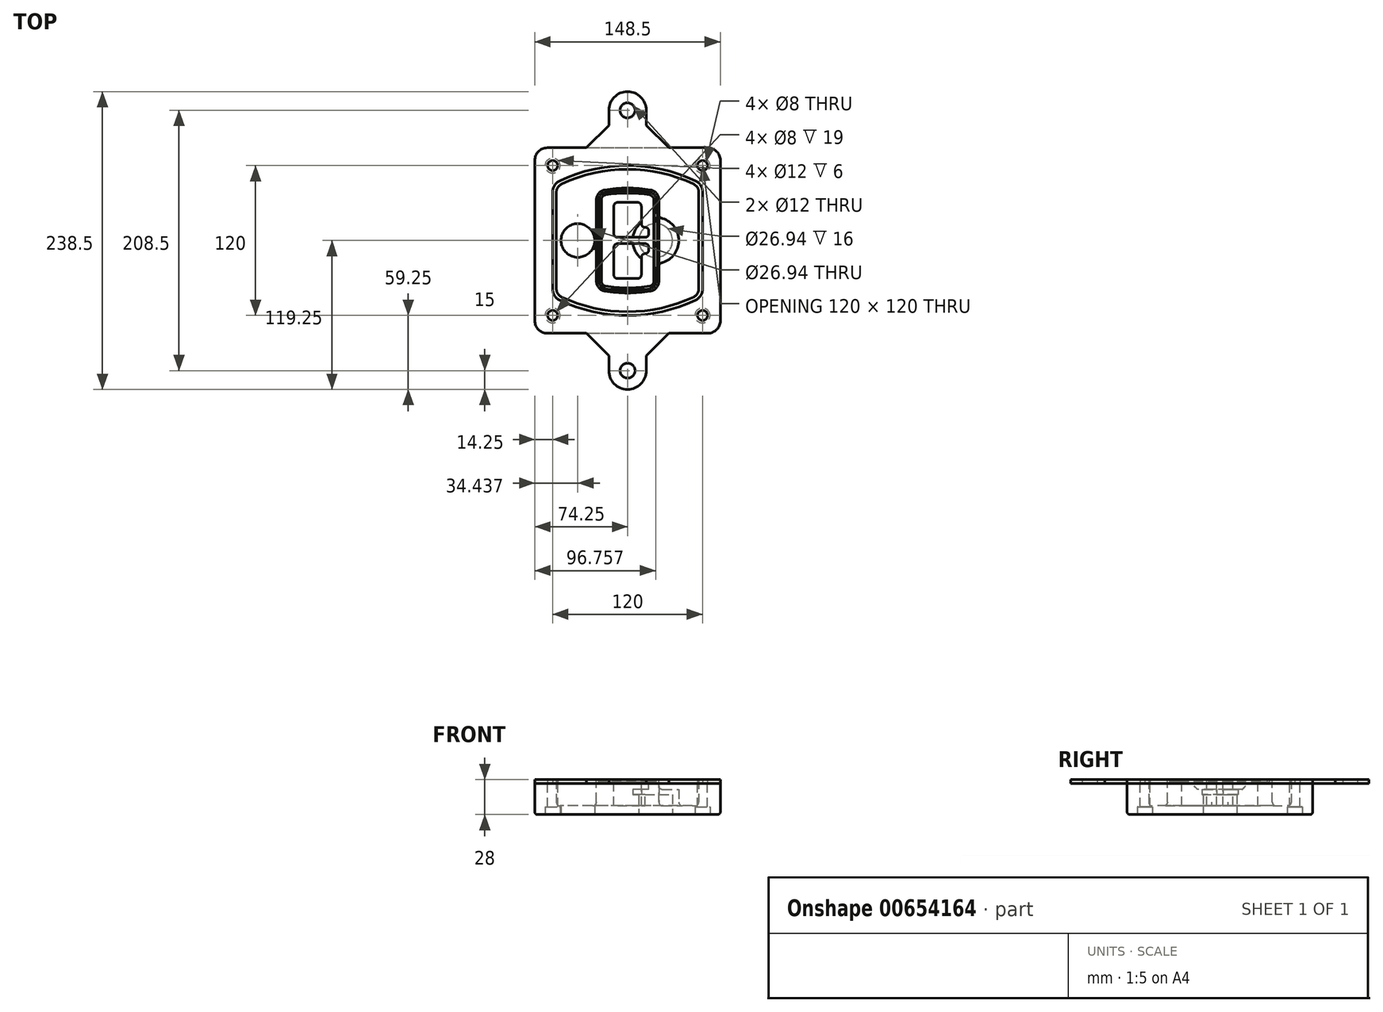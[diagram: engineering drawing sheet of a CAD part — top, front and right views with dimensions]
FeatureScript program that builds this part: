
annotation { "Feature Type Name" : "Feature", "Feature Type Description" : "" }
export const myFeature = defineFeature(function(context is Context, id is Id, definition is map)
    precondition{}
    {
        {
            var Q0;
            Q0=qCreatedBy(makeId("Top.planeOp"),FACE);
            var sketch = newSketch(context, id + "F0", { "sketchPlane" : qUnion([Q0])});
            skPoint(sketch, "E0.rect.middle", {"position": v(0, 0) * mm});
            skLineSegment(sketch, "E1.bottom", {"start": v(-64.25, -74.25) * mm, "end": v(64.25, -74.25) * mm});
            skLineSegment(sketch, "E1.top", {"start": v(-64.25, 74.25) * mm, "end": v(64.25, 74.25) * mm});
            skLineSegment(sketch, "E1.left", {"start": v(-74.25, -64.25) * mm, "end": v(-74.25, 64.25) * mm});
            skLineSegment(sketch, "E1.right", {"start": v(74.25, -64.25) * mm, "end": v(74.25, 64.25) * mm});
            skLineSegment(sketch, "E2", {"start": v(-74.25, 74.25) * mm, "end": v(74.25, -74.25) * mm, "construction": true});
            skLineSegment(sketch, "E3", {"start": v(74.25, 74.25) * mm, "end": v(-74.25, -74.25) * mm, "construction": true});
            skCircle(sketch, "E4", {"center": v(-60, 60) * mm, "radius": 4 * mm});
            skCircle(sketch, "E5", {"center": v(60, 60) * mm, "radius": 4 * mm});
            skCircle(sketch, "E6", {"center": v(60, -60) * mm, "radius": 4 * mm});
            skCircle(sketch, "E7", {"center": v(-60, -60) * mm, "radius": 4 * mm});
            skLineSegment(sketch, "E8", {"start": v(-60, 60) * mm, "end": v(60, 60) * mm, "construction": true});
            skLineSegment(sketch, "E9", {"start": v(60, 60) * mm, "end": v(60, -60) * mm, "construction": true});
            skLineSegment(sketch, "E10", {"start": v(60, -60) * mm, "end": v(-60, -60) * mm, "construction": true});
            skLineSegment(sketch, "E11", {"start": v(-60, -60) * mm, "end": v(-60, 60) * mm, "construction": true});
            skLineSegment(sketch, "E12", {"start": v(-60, 38.83) * mm, "end": v(-60, -38.83) * mm});
            skLineSegment(sketch, "E13", {"start": v(60, 38.83) * mm, "end": v(60, -38.83) * mm});
            skArc(sketch, "E14", {"start": v(54.26, 47.88) * mm, "mid": v(0, 60) * mm, "end": v(-54.26, 47.88) * mm});
            skArc(sketch, "E15", {"start": v(-54.26, -47.88) * mm, "mid": v(0, -60) * mm, "end": v(54.26, -47.88) * mm});
            skLineSegment(sketch, "E16", {"start": v(-60, 0) * mm, "end": v(60, 0) * mm, "construction": true});
            skPoint(sketch, "E17.visualSharp", {"position": v(-60, -45) * mm});
            skArc(sketch, "E17.filletArc", {"start": v(-60, -38.83) * mm, "mid": v(-58.44, -44.2) * mm, "end": v(-54.26, -47.88) * mm});
            skPoint(sketch, "E18.visualSharp", {"position": v(-60, 45) * mm});
            skArc(sketch, "E18.filletArc", {"start": v(-54.26, 47.88) * mm, "mid": v(-58.44, 44.2) * mm, "end": v(-60, 38.83) * mm});
            skPoint(sketch, "E19.visualSharp", {"position": v(60, 45) * mm});
            skArc(sketch, "E19.filletArc", {"start": v(60, 38.83) * mm, "mid": v(58.44, 44.2) * mm, "end": v(54.26, 47.88) * mm});
            skPoint(sketch, "E20.visualSharp", {"position": v(60, -45) * mm});
            skArc(sketch, "E20.filletArc", {"start": v(54.26, -47.88) * mm, "mid": v(58.44, -44.2) * mm, "end": v(60, -38.83) * mm});
            skPoint(sketch, "E21.visualSharp", {"position": v(-74.25, 74.25) * mm});
            skArc(sketch, "E21.filletArc", {"start": v(-64.25, 74.25) * mm, "mid": v(-71.32, 71.32) * mm, "end": v(-74.25, 64.25) * mm});
            skPoint(sketch, "E22.visualSharp", {"position": v(74.25, 74.25) * mm});
            skArc(sketch, "E22.filletArc", {"start": v(74.25, 64.25) * mm, "mid": v(71.32, 71.32) * mm, "end": v(64.25, 74.25) * mm});
            skPoint(sketch, "E23.visualSharp", {"position": v(74.25, -74.25) * mm});
            skArc(sketch, "E23.filletArc", {"start": v(64.25, -74.25) * mm, "mid": v(71.32, -71.32) * mm, "end": v(74.25, -64.25) * mm});
            skPoint(sketch, "E24.visualSharp", {"position": v(-74.25, -74.25) * mm});
            skArc(sketch, "E24.filletArc", {"start": v(-74.25, -64.25) * mm, "mid": v(-71.32, -71.32) * mm, "end": v(-64.25, -74.25) * mm});
            skArc(sketch, "E25.0", {"start": v(57, 38.83) * mm, "mid": v(55.9, 42.58) * mm, "end": v(52.98, 45.17) * mm});
            skLineSegment(sketch, "E25.1", {"start": v(57, 38.83) * mm, "end": v(57, -38.83) * mm});
            skArc(sketch, "E25.2", {"start": v(52.98, -45.17) * mm, "mid": v(55.9, -42.58) * mm, "end": v(57, -38.83) * mm});
            skArc(sketch, "E25.3", {"start": v(-52.98, -45.17) * mm, "mid": v(0, -57) * mm, "end": v(52.98, -45.17) * mm});
            skArc(sketch, "E25.4", {"start": v(-57, -38.83) * mm, "mid": v(-55.9, -42.58) * mm, "end": v(-52.98, -45.17) * mm});
            skArc(sketch, "E25.5", {"start": v(52.98, 45.17) * mm, "mid": v(0, 57) * mm, "end": v(-52.98, 45.17) * mm});
            skLineSegment(sketch, "E25.6", {"start": v(-57, 38.83) * mm, "end": v(-57, -38.83) * mm});
            skArc(sketch, "E25.7", {"start": v(-52.98, 45.17) * mm, "mid": v(-55.9, 42.58) * mm, "end": v(-57, 38.83) * mm});
            skArc(sketch, "E26.0", {"start": v(-55.96, 51.5) * mm, "mid": v(-61.82, 46.33) * mm, "end": v(-64, 38.83) * mm});
            skArc(sketch, "E26.1", {"start": v(55.96, 51.5) * mm, "mid": v(0, 64) * mm, "end": v(-55.96, 51.5) * mm});
            skArc(sketch, "E26.2", {"start": v(64, 38.83) * mm, "mid": v(61.82, 46.33) * mm, "end": v(55.96, 51.5) * mm});
            skLineSegment(sketch, "E26.3", {"start": v(64, 38.83) * mm, "end": v(64, -38.83) * mm});
            skArc(sketch, "E26.4", {"start": v(55.96, -51.5) * mm, "mid": v(61.82, -46.33) * mm, "end": v(64, -38.83) * mm});
            skLineSegment(sketch, "E26.5", {"start": v(-64, 38.83) * mm, "end": v(-64, -38.83) * mm});
            skArc(sketch, "E26.6", {"start": v(-55.96, -51.5) * mm, "mid": v(0, -64) * mm, "end": v(55.96, -51.5) * mm});
            skArc(sketch, "E26.7", {"start": v(-64, -38.83) * mm, "mid": v(-61.82, -46.33) * mm, "end": v(-55.96, -51.5) * mm});
            skLineSegment(sketch, "E27", {"start": v(0, 74.25) * mm, "end": v(0, 104.25) * mm, "construction": true});
            skCircle(sketch, "E28", {"center": v(0, 104.25) * mm, "radius": 6 * mm});
            skArc(sketch, "E29", {"start": v(-15, 104.25) * mm, "mid": v(0, 119.25) * mm, "end": v(15, 104.25) * mm});
            skLineSegment(sketch, "E30", {"start": v(-15, 104.25) * mm, "end": v(-15, 92.25) * mm});
            skLineSegment(sketch, "E31", {"start": v(15, 104.25) * mm, "end": v(15, 92.25) * mm});
            skLineSegment(sketch, "E32", {"start": v(15, 92.25) * mm, "end": v(33, 74.25) * mm});
            skLineSegment(sketch, "E33", {"start": v(-15, 92.25) * mm, "end": v(-33, 74.25) * mm});
            skLineSegment(sketch, "E34", {"start": v(0, -74.25) * mm, "end": v(0, -104.25) * mm, "construction": true});
            skCircle(sketch, "E35", {"center": v(0, -104.25) * mm, "radius": 6 * mm});
            skArc(sketch, "E36", {"start": v(15, -104.25) * mm, "mid": v(0, -119.25) * mm, "end": v(-15, -104.25) * mm});
            skLineSegment(sketch, "E37", {"start": v(15, -104.25) * mm, "end": v(15, -92.25) * mm});
            skLineSegment(sketch, "E38", {"start": v(-15, -104.25) * mm, "end": v(-15, -92.25) * mm});
            skLineSegment(sketch, "E39", {"start": v(-15, -92.25) * mm, "end": v(-33, -74.25) * mm});
            skLineSegment(sketch, "E40", {"start": v(15, -92.25) * mm, "end": v(33, -74.25) * mm});
            skSolve(sketch);
        }
        {
            var Q0;
            Q0=makeQuery(id+"F0.imprint","IMPRINT",FACE,{"disambiguationData":[TD([[makeQuery(id+"F0.imprint","IMPRINT",EDGE,{"derivedFrom":sQuery(id+"F0.wireOp",EDGE,"E1.bottom")}),1.0]])]});
            var Q1;
            Q1=makeQuery(id+"F0.imprint","IMPRINT",FACE,{"disambiguationData":[TD([[makeQuery(id+"F0.imprint","IMPRINT",EDGE,{"derivedFrom":sQuery(id+"F0.wireOp",EDGE,"E12")}),1.0]])]});
            var Q2;
            Q2=makeQuery(id+"F0.imprint","IMPRINT",FACE,{"disambiguationData":[TD([[makeQuery(id+"F0.imprint","IMPRINT",EDGE,{"derivedFrom":sQuery(id+"F0.wireOp",EDGE,"E25.0")}),1.0]])]});
            var Q3;
            Q3=makeQuery(id+"F0.imprint","IMPRINT",FACE,{"disambiguationData":[TD([[makeQuery(id+"F0.imprint","IMPRINT",EDGE,{"derivedFrom":sQuery(id+"F0.wireOp",EDGE,"E12")}),-1.0]])]});
            extrude(context, id + "F1", {"entities" : qUnion([Q0, Q1, Q2, Q3]), "oppositeDirection" : true, "depth" : 25 * mm});
        }
        {
            var Q0;
            Q0=makeQuery(id+"F0.imprint","IMPRINT",FACE,{"disambiguationData":[TD([[makeQuery(id+"F0.imprint","IMPRINT",EDGE,{"derivedFrom":sQuery(id+"F0.wireOp",EDGE,"E12")}),1.0]])]});
            extrude(context, id + "F2", {"entities" : qUnion([Q0]), "operationType" : NewBodyOperationType.ADD, "depth" : 3 * mm});
        }
        {
            var Q0;
            Q0=makeQuery(id+"F0.imprint","IMPRINT",FACE,{"disambiguationData":[TD([[makeQuery(id+"F0.imprint","IMPRINT",EDGE,{"derivedFrom":sQuery(id+"F0.wireOp",EDGE,"E25.0")}),1.0]])]});
            extrude(context, id + "F3", {"entities" : qUnion([Q0]), "operationType" : NewBodyOperationType.REMOVE, "oppositeDirection" : true, "depth" : 18 * mm});
        }
        {
            var Q0;
            Q0=makeQuery(id+"F2.opExtrude","CAP_FACE",FACE,{"disambiguationData":[OSD([sQuery(id+"F0.wireOp",EDGE,"E12"),sQuery(id+"F0.wireOp",EDGE,"E13"),sQuery(id+"F0.wireOp",EDGE,"E14"),sQuery(id+"F0.wireOp",EDGE,"E15"),sQuery(id+"F0.wireOp",EDGE,"E17.filletArc"),sQuery(id+"F0.wireOp",EDGE,"E18.filletArc"),sQuery(id+"F0.wireOp",EDGE,"E19.filletArc"),sQuery(id+"F0.wireOp",EDGE,"E20.filletArc"),sQuery(id+"F0.wireOp",EDGE,"E25.0"),sQuery(id+"F0.wireOp",EDGE,"E25.1"),sQuery(id+"F0.wireOp",EDGE,"E25.2"),sQuery(id+"F0.wireOp",EDGE,"E25.3"),sQuery(id+"F0.wireOp",EDGE,"E25.4"),sQuery(id+"F0.wireOp",EDGE,"E25.5"),sQuery(id+"F0.wireOp",EDGE,"E25.6"),sQuery(id+"F0.wireOp",EDGE,"E25.7")])],"isStart":false});
            var sketch = newSketch(context, id + "F4", { "sketchPlane" : qUnion([Q0])});
            skArc(sketch, "E41.0", {"start": v(-18.34, -40.45) * mm, "mid": v(0, -42) * mm, "end": v(18.34, -40.45) * mm});
            skArc(sketch, "E42.0", {"start": v(18.34, 40.45) * mm, "mid": v(0, 42) * mm, "end": v(-18.34, 40.45) * mm});
            skLineSegment(sketch, "E43", {"start": v(-25, 32.57) * mm, "end": v(-25, -32.57) * mm});
            skLineSegment(sketch, "E44", {"start": v(25, 32.57) * mm, "end": v(25, -32.57) * mm});
            skLineSegment(sketch, "E45", {"start": v(-25, 39.1) * mm, "end": v(25, 39.1) * mm, "construction": true});
            skLineSegment(sketch, "E46", {"start": v(-25, -39.1) * mm, "end": v(25, -39.1) * mm, "construction": true});
            skPoint(sketch, "E47.visualSharp", {"position": v(-25, 39.1) * mm});
            skArc(sketch, "E47.filletArc", {"start": v(-18.34, 40.45) * mm, "mid": v(-23.11, 37.73) * mm, "end": v(-25, 32.57) * mm});
            skPoint(sketch, "E48.visualSharp", {"position": v(25, 39.1) * mm});
            skArc(sketch, "E48.filletArc", {"start": v(25, 32.57) * mm, "mid": v(23.11, 37.73) * mm, "end": v(18.34, 40.45) * mm});
            skPoint(sketch, "E49.visualSharp", {"position": v(25, -39.1) * mm});
            skArc(sketch, "E49.filletArc", {"start": v(18.34, -40.45) * mm, "mid": v(23.11, -37.73) * mm, "end": v(25, -32.57) * mm});
            skPoint(sketch, "E50.visualSharp", {"position": v(-25, -39.1) * mm});
            skArc(sketch, "E50.filletArc", {"start": v(-25, -32.57) * mm, "mid": v(-23.11, -37.73) * mm, "end": v(-18.34, -40.45) * mm});
            skArc(sketch, "E51.0", {"start": v(52.98, 45.17) * mm, "mid": v(0, 57) * mm, "end": v(-52.98, 45.17) * mm});
            skArc(sketch, "E51.1", {"start": v(-52.98, 45.17) * mm, "mid": v(-55.9, 42.58) * mm, "end": v(-57, 38.83) * mm});
            skLineSegment(sketch, "E51.2", {"start": v(-57, 38.83) * mm, "end": v(-57, -38.83) * mm});
            skArc(sketch, "E51.3", {"start": v(-57, -38.83) * mm, "mid": v(-55.9, -42.58) * mm, "end": v(-52.98, -45.17) * mm});
            skArc(sketch, "E51.4", {"start": v(-52.98, -45.17) * mm, "mid": v(0, -57) * mm, "end": v(52.98, -45.17) * mm});
            skArc(sketch, "E51.5", {"start": v(52.98, -45.17) * mm, "mid": v(55.9, -42.58) * mm, "end": v(57, -38.83) * mm});
            skLineSegment(sketch, "E51.6", {"start": v(57, 38.83) * mm, "end": v(57, -38.83) * mm});
            skArc(sketch, "E51.7", {"start": v(57, 38.83) * mm, "mid": v(55.9, 42.58) * mm, "end": v(52.98, 45.17) * mm});
            skLineSegment(sketch, "E52.0", {"start": v(23, 32.57) * mm, "end": v(23, -32.57) * mm});
            skArc(sketch, "E52.1", {"start": v(18, -38.48) * mm, "mid": v(21.58, -36.44) * mm, "end": v(23, -32.57) * mm});
            skArc(sketch, "E52.2", {"start": v(-18, -38.48) * mm, "mid": v(0, -40) * mm, "end": v(18, -38.48) * mm});
            skArc(sketch, "E52.3", {"start": v(-23, -32.57) * mm, "mid": v(-21.58, -36.44) * mm, "end": v(-18, -38.48) * mm});
            skLineSegment(sketch, "E52.4", {"start": v(-23, 32.57) * mm, "end": v(-23, -32.57) * mm});
            skArc(sketch, "E52.5", {"start": v(23, 32.57) * mm, "mid": v(21.58, 36.44) * mm, "end": v(18, 38.48) * mm});
            skArc(sketch, "E52.6", {"start": v(-18, 38.48) * mm, "mid": v(-21.58, 36.44) * mm, "end": v(-23, 32.57) * mm});
            skArc(sketch, "E52.7", {"start": v(18, 38.48) * mm, "mid": v(0, 40) * mm, "end": v(-18, 38.48) * mm});
            skArc(sketch, "E53.0", {"start": v(21, 32.57) * mm, "mid": v(20.06, 35.15) * mm, "end": v(17.67, 36.5) * mm});
            skLineSegment(sketch, "E53.1", {"start": v(21, 32.57) * mm, "end": v(21, -32.57) * mm});
            skArc(sketch, "E53.2", {"start": v(17.67, -36.5) * mm, "mid": v(20.06, -35.15) * mm, "end": v(21, -32.57) * mm});
            skArc(sketch, "E53.3", {"start": v(-17.67, -36.5) * mm, "mid": v(0, -38) * mm, "end": v(17.67, -36.5) * mm});
            skArc(sketch, "E53.4", {"start": v(-21, -32.57) * mm, "mid": v(-20.06, -35.15) * mm, "end": v(-17.67, -36.5) * mm});
            skArc(sketch, "E53.5", {"start": v(17.67, 36.5) * mm, "mid": v(0, 38) * mm, "end": v(-17.67, 36.5) * mm});
            skLineSegment(sketch, "E53.6", {"start": v(-21, 32.57) * mm, "end": v(-21, -32.57) * mm});
            skArc(sketch, "E53.7", {"start": v(-17.67, 36.5) * mm, "mid": v(-20.06, 35.15) * mm, "end": v(-21, 32.57) * mm});
            skLineSegment(sketch, "E54", {"start": v(-25, 0) * mm, "end": v(25, 0) * mm, "construction": true});
            skLineSegment(sketch, "E55", {"start": v(-11, 5.5) * mm, "end": v(-11, 27.5) * mm});
            skLineSegment(sketch, "E56", {"start": v(-8, 30.5) * mm, "end": v(8, 30.5) * mm});
            skLineSegment(sketch, "E57", {"start": v(11, 27.5) * mm, "end": v(11, 13.5) * mm});
            skLineSegment(sketch, "E58", {"start": v(14, 10.5) * mm, "end": v(14, 10.5) * mm});
            skLineSegment(sketch, "E59", {"start": v(17, 7.5) * mm, "end": v(17, 5.5) * mm});
            skLineSegment(sketch, "E60", {"start": v(14, 2.5) * mm, "end": v(-8, 2.5) * mm});
            skPoint(sketch, "E61.visualSharp", {"position": v(-11, 30.5) * mm});
            skArc(sketch, "E61.filletArc", {"start": v(-8, 30.5) * mm, "mid": v(-10.12, 29.62) * mm, "end": v(-11, 27.5) * mm});
            skPoint(sketch, "E62.visualSharp", {"position": v(11, 30.5) * mm});
            skArc(sketch, "E62.filletArc", {"start": v(11, 27.5) * mm, "mid": v(10.12, 29.62) * mm, "end": v(8, 30.5) * mm});
            skPoint(sketch, "E63.visualSharp", {"position": v(11, 10.5) * mm});
            skArc(sketch, "E63.filletArc", {"start": v(11, 13.5) * mm, "mid": v(11.88, 11.38) * mm, "end": v(14, 10.5) * mm});
            skPoint(sketch, "E64.visualSharp", {"position": v(17, 10.5) * mm});
            skArc(sketch, "E64.filletArc", {"start": v(17, 7.5) * mm, "mid": v(16.12, 9.62) * mm, "end": v(14, 10.5) * mm});
            skPoint(sketch, "E65.visualSharp", {"position": v(17, 2.5) * mm});
            skArc(sketch, "E65.filletArc", {"start": v(14, 2.5) * mm, "mid": v(16.12, 3.38) * mm, "end": v(17, 5.5) * mm});
            skPoint(sketch, "E66.visualSharp", {"position": v(-11, 2.5) * mm});
            skArc(sketch, "E66.filletArc", {"start": v(-11, 5.5) * mm, "mid": v(-10.12, 3.38) * mm, "end": v(-8, 2.5) * mm});
            skLineSegment(sketch, "E67.0.MirrorCS", {"start": v(14, -2.5) * mm, "end": v(-8, -2.5) * mm});
            skArc(sketch, "E68.0.MirrorCS", {"start": v(-11, -5.5) * mm, "mid": v(-10.12, -3.38) * mm, "end": v(-8, -2.5) * mm});
            skLineSegment(sketch, "E69.0.MirrorCS", {"start": v(-11, -5.5) * mm, "end": v(-11, -27.5) * mm});
            skArc(sketch, "E70.0.MirrorCS", {"start": v(-8, -30.5) * mm, "mid": v(-10.12, -29.62) * mm, "end": v(-11, -27.5) * mm});
            skLineSegment(sketch, "E71.0.MirrorCS", {"start": v(-8, -30.5) * mm, "end": v(8, -30.5) * mm});
            skArc(sketch, "E72.0.MirrorCS", {"start": v(11, -27.5) * mm, "mid": v(10.12, -29.62) * mm, "end": v(8, -30.5) * mm});
            skLineSegment(sketch, "E73.0.MirrorCS", {"start": v(11, -27.5) * mm, "end": v(11, -13.5) * mm});
            skArc(sketch, "E74.0.MirrorCS", {"start": v(11, -13.5) * mm, "mid": v(11.88, -11.38) * mm, "end": v(14, -10.5) * mm});
            skArc(sketch, "E75.0.MirrorCS", {"start": v(17, -7.5) * mm, "mid": v(16.12, -9.62) * mm, "end": v(14, -10.5) * mm});
            skLineSegment(sketch, "E76.0.MirrorCS", {"start": v(17, -7.5) * mm, "end": v(17, -5.5) * mm});
            skArc(sketch, "E77.0.MirrorCS", {"start": v(14, -2.5) * mm, "mid": v(16.12, -3.38) * mm, "end": v(17, -5.5) * mm});
            skSolve(sketch);
        }
        {
            var Q0;
            Q0=makeQuery(id+"F4.imprint","IMPRINT",FACE,{"disambiguationData":[TD([[makeQuery(id+"F4.imprint","IMPRINT",EDGE,{"derivedFrom":sQuery(id+"F4.wireOp",EDGE,"E41.0")}),1.0]])]});
            var Q1;
            Q1=makeQuery(id+"F4.imprint","IMPRINT",FACE,{"disambiguationData":[TD([[makeQuery(id+"F4.imprint","IMPRINT",EDGE,{"derivedFrom":sQuery(id+"F4.wireOp",EDGE,"E52.0")}),-1.0]])]});
            var Q2;
            Q2=makeQuery(id+"F4.imprint","IMPRINT",FACE,{"disambiguationData":[TD([[makeQuery(id+"F4.imprint","IMPRINT",EDGE,{"derivedFrom":sQuery(id+"F4.wireOp",EDGE,"E53.0")}),1.0]])]});
            extrude(context, id + "F5", {"entities" : qUnion([Q0, Q1, Q2]), "operationType" : NewBodyOperationType.ADD, "endBound" : BoundingType.UP_TO_NEXT, "oppositeDirection" : true, "depth" : 25 * mm});
        }
        {
            var Q0;
            Q0=makeQuery(id+"F4.imprint","IMPRINT",FACE,{"disambiguationData":[TD([[makeQuery(id+"F4.imprint","IMPRINT",EDGE,{"derivedFrom":sQuery(id+"F4.wireOp",EDGE,"E52.0")}),-1.0]])]});
            extrude(context, id + "F6", {"entities" : qUnion([Q0]), "operationType" : NewBodyOperationType.REMOVE, "oppositeDirection" : true, "depth" : 2 * mm});
        }
        {
            var Q0;
            Q0=makeQuery(id+"F1.opExtrude","CAP_FACE",FACE,{"disambiguationData":[OSD([sQuery(id+"F0.wireOp",EDGE,"E1.bottom"),sQuery(id+"F0.wireOp",EDGE,"E1.top"),sQuery(id+"F0.wireOp",EDGE,"E1.left"),sQuery(id+"F0.wireOp",EDGE,"E1.right"),sQuery(id+"F0.wireOp",EDGE,"E4"),sQuery(id+"F0.wireOp",EDGE,"E5"),sQuery(id+"F0.wireOp",EDGE,"E6"),sQuery(id+"F0.wireOp",EDGE,"E7"),sQuery(id+"F0.wireOp",EDGE,"E21.filletArc"),sQuery(id+"F0.wireOp",EDGE,"E22.filletArc"),sQuery(id+"F0.wireOp",EDGE,"E23.filletArc"),sQuery(id+"F0.wireOp",EDGE,"E24.filletArc")])],"isStart":false});
            var sketch = newSketch(context, id + "F7", { "sketchPlane" : qUnion([Q0])});
            skCircle(sketch, "E78", {"center": v(22.5, 0) * mm, "radius": 13.47 * mm});
            skCircle(sketch, "E79", {"center": v(-39.81, 0) * mm, "radius": 13.47 * mm});
            skLineSegment(sketch, "E80", {"start": v(74.25, 0) * mm, "end": v(-74.25, 0) * mm});
            skCircle(sketch, "E81", {"center": v(22.5, 0) * mm, "radius": 18.47 * mm});
            skCircle(sketch, "E82", {"center": v(60, -60) * mm, "radius": 6 * mm});
            skCircle(sketch, "E83", {"center": v(-60, -60) * mm, "radius": 6 * mm});
            skCircle(sketch, "E84", {"center": v(-60, 60) * mm, "radius": 6 * mm});
            skCircle(sketch, "E85", {"center": v(60, 60) * mm, "radius": 6 * mm});
            skSolve(sketch);
        }
        {
            var Q0;
            {var subQ1=sQuery(id+"F7.wireOp",EDGE,"E80");var subQ4=sQuery(id+"F7.wireOp",EDGE,"E78");var subQ6=makeQuery(id+"F7.imprint","INTERSECT",VERTEX,{"disambiguationData":[OD(0.0)],"derivedFrom":[subQ4,subQ1]});Q0=makeQuery(id+"F7.imprint","IMPRINT",FACE,{"disambiguationData":[TD([[makeQuery(id+"F7.imprint","IMPRINT",EDGE,{"disambiguationData":[TD([[subQ6,-1.0]])],"derivedFrom":subQ4}),-1.0]])]});}
            var Q1;
            {var subQ0=sQuery(id+"F7.wireOp",EDGE,"E80");var subQ1=sQuery(id+"F7.wireOp",EDGE,"E78");var subQ3=makeQuery(id+"F7.imprint","INTERSECT",VERTEX,{"disambiguationData":[OD(0.0)],"derivedFrom":[subQ1,subQ0]});Q1=makeQuery(id+"F7.imprint","IMPRINT",FACE,{"disambiguationData":[TD([[makeQuery(id+"F7.imprint","IMPRINT",EDGE,{"disambiguationData":[TD([[subQ3,-1.0]])],"derivedFrom":subQ1}),1.0]])]});}
            var Q2;
            {var subQ0=sQuery(id+"F7.wireOp",EDGE,"E80");var subQ1=sQuery(id+"F7.wireOp",EDGE,"E78");var subQ3=makeQuery(id+"F7.imprint","INTERSECT",VERTEX,{"disambiguationData":[OD(0.0)],"derivedFrom":[subQ1,subQ0]});Q2=makeQuery(id+"F7.imprint","IMPRINT",FACE,{"disambiguationData":[TD([[makeQuery(id+"F7.imprint","IMPRINT",EDGE,{"disambiguationData":[TD([[subQ3,1.0]])],"derivedFrom":subQ1}),1.0]])]});}
            var Q3;
            {var subQ1=sQuery(id+"F7.wireOp",EDGE,"E80");var subQ4=sQuery(id+"F7.wireOp",EDGE,"E78");var subQ6=makeQuery(id+"F7.imprint","INTERSECT",VERTEX,{"disambiguationData":[OD(0.0)],"derivedFrom":[subQ4,subQ1]});Q3=makeQuery(id+"F7.imprint","IMPRINT",FACE,{"disambiguationData":[TD([[makeQuery(id+"F7.imprint","IMPRINT",EDGE,{"disambiguationData":[TD([[subQ6,1.0]])],"derivedFrom":subQ4}),-1.0]])]});}
            extrude(context, id + "F8", {"entities" : qUnion([Q0, Q1, Q2, Q3]), "operationType" : NewBodyOperationType.ADD, "oppositeDirection" : true, "depth" : 20 * mm});
        }
        {
            var Q0;
            {var subQ0=sQuery(id+"F7.wireOp",EDGE,"E80");var subQ1=sQuery(id+"F7.wireOp",EDGE,"E78");var subQ3=makeQuery(id+"F7.imprint","INTERSECT",VERTEX,{"disambiguationData":[OD(0.0)],"derivedFrom":[subQ1,subQ0]});Q0=makeQuery(id+"F7.imprint","IMPRINT",FACE,{"disambiguationData":[TD([[makeQuery(id+"F7.imprint","IMPRINT",EDGE,{"disambiguationData":[TD([[subQ3,-1.0]])],"derivedFrom":subQ1}),1.0]])]});}
            var Q1;
            {var subQ0=sQuery(id+"F7.wireOp",EDGE,"E80");var subQ1=sQuery(id+"F7.wireOp",EDGE,"E78");var subQ3=makeQuery(id+"F7.imprint","INTERSECT",VERTEX,{"disambiguationData":[OD(0.0)],"derivedFrom":[subQ1,subQ0]});Q1=makeQuery(id+"F7.imprint","IMPRINT",FACE,{"disambiguationData":[TD([[makeQuery(id+"F7.imprint","IMPRINT",EDGE,{"disambiguationData":[TD([[subQ3,1.0]])],"derivedFrom":subQ1}),1.0]])]});}
            extrude(context, id + "F9", {"entities" : qUnion([Q0, Q1]), "operationType" : NewBodyOperationType.REMOVE, "oppositeDirection" : true, "depth" : 16 * mm});
        }
        {
            var Q0;
            {var subQ0=sQuery(id+"F7.wireOp",EDGE,"E80");var subQ1=sQuery(id+"F7.wireOp",EDGE,"E79");var subQ3=makeQuery(id+"F7.imprint","INTERSECT",VERTEX,{"disambiguationData":[OD(0.0)],"derivedFrom":[subQ1,subQ0]});Q0=makeQuery(id+"F7.imprint","IMPRINT",FACE,{"disambiguationData":[TD([[makeQuery(id+"F7.imprint","IMPRINT",EDGE,{"disambiguationData":[TD([[subQ3,-1.0]])],"derivedFrom":subQ1}),1.0]])]});}
            var Q1;
            {var subQ0=sQuery(id+"F7.wireOp",EDGE,"E80");var subQ1=sQuery(id+"F7.wireOp",EDGE,"E79");var subQ3=makeQuery(id+"F7.imprint","INTERSECT",VERTEX,{"disambiguationData":[OD(0.0)],"derivedFrom":[subQ1,subQ0]});Q1=makeQuery(id+"F7.imprint","IMPRINT",FACE,{"disambiguationData":[TD([[makeQuery(id+"F7.imprint","IMPRINT",EDGE,{"disambiguationData":[TD([[subQ3,1.0]])],"derivedFrom":subQ1}),1.0]])]});}
            extrude(context, id + "F10", {"entities" : qUnion([Q0, Q1]), "operationType" : NewBodyOperationType.REMOVE, "oppositeDirection" : true, "depth" : 25 * mm});
        }
        {
            var Q0;
            Q0=makeQuery(id+"F7.imprint","IMPRINT",FACE,{"disambiguationData":[TD([[makeQuery(id+"F7.imprint","IMPRINT",EDGE,{"derivedFrom":sQuery(id+"F7.wireOp",EDGE,"E82")}),1.0]])]});
            var Q1;
            Q1=makeQuery(id+"F7.imprint","IMPRINT",FACE,{"disambiguationData":[TD([[makeQuery(id+"F7.imprint","IMPRINT",EDGE,{"derivedFrom":makeQuery(id+"F1.opExtrude","CAP_EDGE",EDGE,{"disambiguationData":[OSD([sQuery(id+"F0.wireOp",EDGE,"E5")])],"isStart":false})}),-1.0]])]});
            var Q2;
            Q2=makeQuery(id+"F7.imprint","IMPRINT",FACE,{"disambiguationData":[TD([[makeQuery(id+"F7.imprint","IMPRINT",EDGE,{"derivedFrom":sQuery(id+"F7.wireOp",EDGE,"E83")}),1.0]])]});
            var Q3;
            Q3=makeQuery(id+"F7.imprint","IMPRINT",FACE,{"disambiguationData":[TD([[makeQuery(id+"F7.imprint","IMPRINT",EDGE,{"derivedFrom":makeQuery(id+"F1.opExtrude","CAP_EDGE",EDGE,{"disambiguationData":[OSD([sQuery(id+"F0.wireOp",EDGE,"E4")])],"isStart":false})}),-1.0]])]});
            var Q4;
            Q4=makeQuery(id+"F7.imprint","IMPRINT",FACE,{"disambiguationData":[TD([[makeQuery(id+"F7.imprint","IMPRINT",EDGE,{"derivedFrom":sQuery(id+"F7.wireOp",EDGE,"E84")}),1.0]])]});
            var Q5;
            Q5=makeQuery(id+"F7.imprint","IMPRINT",FACE,{"disambiguationData":[TD([[makeQuery(id+"F7.imprint","IMPRINT",EDGE,{"derivedFrom":makeQuery(id+"F1.opExtrude","CAP_EDGE",EDGE,{"disambiguationData":[OSD([sQuery(id+"F0.wireOp",EDGE,"E7")])],"isStart":false})}),-1.0]])]});
            var Q6;
            Q6=makeQuery(id+"F7.imprint","IMPRINT",FACE,{"disambiguationData":[TD([[makeQuery(id+"F7.imprint","IMPRINT",EDGE,{"derivedFrom":sQuery(id+"F7.wireOp",EDGE,"E85")}),1.0]])]});
            var Q7;
            Q7=makeQuery(id+"F7.imprint","IMPRINT",FACE,{"disambiguationData":[TD([[makeQuery(id+"F7.imprint","IMPRINT",EDGE,{"derivedFrom":makeQuery(id+"F1.opExtrude","CAP_EDGE",EDGE,{"disambiguationData":[OSD([sQuery(id+"F0.wireOp",EDGE,"E6")])],"isStart":false})}),-1.0]])]});
            extrude(context, id + "F11", {"entities" : qUnion([Q0, Q1, Q2, Q3, Q4, Q5, Q6, Q7]), "operationType" : NewBodyOperationType.REMOVE, "oppositeDirection" : true, "depth" : 6 * mm});
        }
        {
            var Q0;
            Q0=makeQuery(id+"F9.boolean.opBoolean","COPY",FACE,{"derivedFrom":makeQuery(id+"F9.opExtrude","CAP_FACE",FACE,{"disambiguationData":[OSD([sQuery(id+"F7.wireOp",EDGE,"E78")])],"isStart":false})});
            var sketch = newSketch(context, id + "F12", { "sketchPlane" : qUnion([Q0])});
            skArc(sketch, "E86.0", {"start": v(11, 14.45) * mm, "mid": v(6.45, 9.13) * mm, "end": v(4.2, 2.5) * mm});
            skArc(sketch, "E86.1", {"start": v(4.2, -2.5) * mm, "mid": v(6.45, -9.13) * mm, "end": v(11, -14.45) * mm});
            skLineSegment(sketch, "E87", {"start": v(4.2, -2.5) * mm, "end": v(14, -2.5) * mm});
            skLineSegment(sketch, "E88.0", {"start": v(14, 2.5) * mm, "end": v(4.2, 2.5) * mm});
            skArc(sketch, "E88.1", {"start": v(14, 2.5) * mm, "mid": v(16.12, 3.38) * mm, "end": v(17, 5.5) * mm});
            skLineSegment(sketch, "E88.2", {"start": v(17, 7.5) * mm, "end": v(17, 5.5) * mm});
            skArc(sketch, "E88.3", {"start": v(17, 7.5) * mm, "mid": v(16.12, 9.62) * mm, "end": v(14, 10.5) * mm});
            skArc(sketch, "E88.4", {"start": v(11, 13.5) * mm, "mid": v(11.88, 11.38) * mm, "end": v(14, 10.5) * mm});
            skLineSegment(sketch, "E88.5", {"start": v(11, 14.45) * mm, "end": v(11, 13.5) * mm});
            skLineSegment(sketch, "E88.7", {"start": v(14, -2.5) * mm, "end": v(4.2, -2.5) * mm});
            skArc(sketch, "E88.8", {"start": v(14, -2.5) * mm, "mid": v(16.12, -3.38) * mm, "end": v(17, -5.5) * mm});
            skLineSegment(sketch, "E88.9", {"start": v(17, -7.5) * mm, "end": v(17, -5.5) * mm});
            skArc(sketch, "E88.10", {"start": v(17, -7.5) * mm, "mid": v(16.12, -9.62) * mm, "end": v(14, -10.5) * mm});
            skArc(sketch, "E88.11", {"start": v(11, -13.5) * mm, "mid": v(11.88, -11.38) * mm, "end": v(14, -10.5) * mm});
            skLineSegment(sketch, "E88.12", {"start": v(11, -14.45) * mm, "end": v(11, -13.5) * mm});
            skPoint(sketch, "E89.orphan", {"position": v(11, -27.5) * mm});
            skPoint(sketch, "E90.orphan", {"position": v(-8, -2.5) * mm});
            skPoint(sketch, "E91.orphan", {"position": v(-8, 2.5) * mm});
            skPoint(sketch, "E92.orphan", {"position": v(11, 27.5) * mm});
            skSolve(sketch);
        }
        {
            var Q0;
            {var subQ7=sQuery(id+"F12.wireOp",EDGE,"E86.0");var subQ14=sQuery(id+"F12.wireOp",EDGE,"E86.1");var subQ16=sQuery(id+"F12.wireOp",EDGE,"E88.1");var subQ18=sQuery(id+"F12.wireOp",EDGE,"E88.8");Q0=qUnion([makeQuery(id+"F12.imprint","IMPRINT",FACE,{"disambiguationData":[TD([[makeQuery(id+"F12.imprint","IMPRINT",EDGE,{"derivedFrom":subQ7}),1.0]])]}),makeQuery(id+"F12.imprint","IMPRINT",FACE,{"disambiguationData":[TD([[makeQuery(id+"F12.imprint","IMPRINT",EDGE,{"derivedFrom":subQ14}),1.0]])]}),makeQuery(id+"F12.imprint","IMPRINT",FACE,{"disambiguationData":[TD([[makeQuery(id+"F12.imprint","IMPRINT",EDGE,{"derivedFrom":subQ16}),1.0]])]}),makeQuery(id+"F12.imprint","IMPRINT",FACE,{"disambiguationData":[TD([[makeQuery(id+"F12.imprint","IMPRINT",EDGE,{"derivedFrom":subQ18}),-1.0]])]})]);}
            var Q1;
            Q1=makeQuery(id+"F5.boolean.opBoolean","SPLIT",FACE,{"disambiguationData":[TD([makeQuery(id+"F5.opExtrude","SWEPT_FACE",FACE,{"disambiguationData":[OSD([sQuery(id+"F4.wireOp",EDGE,"E55")])]})])],"derivedFrom":makeQuery(id+"F3.boolean.opBoolean","COPY",FACE,{"derivedFrom":makeQuery(id+"F3.opExtrude","CAP_FACE",FACE,{"disambiguationData":[OSD([sQuery(id+"F0.wireOp",EDGE,"E25.0"),sQuery(id+"F0.wireOp",EDGE,"E25.1"),sQuery(id+"F0.wireOp",EDGE,"E25.2"),sQuery(id+"F0.wireOp",EDGE,"E25.3"),sQuery(id+"F0.wireOp",EDGE,"E25.4"),sQuery(id+"F0.wireOp",EDGE,"E25.5"),sQuery(id+"F0.wireOp",EDGE,"E25.6"),sQuery(id+"F0.wireOp",EDGE,"E25.7")])],"isStart":false})})});
            extrude(context, id + "F13", {"entities" : qUnion([Q0]), "operationType" : NewBodyOperationType.REMOVE, "endBound" : BoundingType.UP_TO_SURFACE, "endBoundEntityFace" : qUnion([Q1]), "depth" : 25 * mm});
        }
        {
            var Q0;
            Q0=makeQuery(id+"F3.boolean.opBoolean","COPY",EDGE,{"derivedFrom":makeQuery(id+"F3.opExtrude","CAP_EDGE",EDGE,{"disambiguationData":[OSD([sQuery(id+"F0.wireOp",EDGE,"E25.6")])],"isStart":false})});
            var Q1;
            Q1=makeQuery(id+"F8.boolean.opBoolean","INTERSECT",EDGE,{"derivedFrom":[makeQuery(id+"F5.opExtrude","SWEPT_FACE",FACE,{"disambiguationData":[OSD([sQuery(id+"F4.wireOp",EDGE,"E44")])]}),makeQuery(id+"F8.opExtrude","CAP_FACE",FACE,{"disambiguationData":[OSD([sQuery(id+"F7.wireOp",EDGE,"E81")])],"isStart":false})]});
            var Q2;
            Q2=makeQuery(id+"F8.boolean.opBoolean","INTERSECT",EDGE,{"disambiguationData":[OD(1.0)],"derivedFrom":[makeQuery(id+"F5.opExtrude","SWEPT_FACE",FACE,{"disambiguationData":[OSD([sQuery(id+"F4.wireOp",EDGE,"E44")])]}),makeQuery(id+"F8.opExtrude","SWEPT_FACE",FACE,{"disambiguationData":[OSD([sQuery(id+"F7.wireOp",EDGE,"E81")])]})]});
            var Q3;
            {var subQ0=sQuery(id+"F4.wireOp",EDGE,"E44");Q3=makeQuery(id+"F8.boolean.opBoolean","SPLIT",EDGE,{"disambiguationData":[TD([makeQuery(id+"F5.opExtrude","SWEPT_FACE",FACE,{"disambiguationData":[OSD([sQuery(id+"F4.wireOp",EDGE,"E49.filletArc")])]})])],"derivedFrom":makeQuery(id+"F5.opExtrude","CAP_EDGE",EDGE,{"disambiguationData":[OSD([subQ0])],"isStart":false})});}
            var Q4;
            {var subQ0=sQuery(id+"F0.wireOp",EDGE,"E25.7");var subQ1=sQuery(id+"F0.wireOp",EDGE,"E25.1");var subQ2=sQuery(id+"F0.wireOp",EDGE,"E25.6");var subQ3=sQuery(id+"F0.wireOp",EDGE,"E25.5");var subQ4=sQuery(id+"F0.wireOp",EDGE,"E25.4");var subQ5=sQuery(id+"F0.wireOp",EDGE,"E25.0");var subQ6=sQuery(id+"F0.wireOp",EDGE,"E25.2");var subQ7=sQuery(id+"F0.wireOp",EDGE,"E25.3");Q4=makeQuery(id+"F8.boolean.opBoolean","INTERSECT",EDGE,{"derivedFrom":[makeQuery(id+"F5.boolean.opBoolean","SPLIT",FACE,{"disambiguationData":[TD([makeQuery(id+"F2.opExtrude","SWEPT_FACE",FACE,{"disambiguationData":[OSD([subQ5])]})])],"derivedFrom":makeQuery(id+"F3.boolean.opBoolean","COPY",FACE,{"derivedFrom":makeQuery(id+"F3.opExtrude","CAP_FACE",FACE,{"disambiguationData":[OSD([subQ5,subQ1,subQ6,subQ7,subQ4,subQ3,subQ2,subQ0])],"isStart":false})})}),makeQuery(id+"F8.opExtrude","SWEPT_FACE",FACE,{"disambiguationData":[OSD([sQuery(id+"F7.wireOp",EDGE,"E81")])]})]});}
            var Q5;
            Q5=makeQuery(id+"F8.boolean.opBoolean","INTERSECT",EDGE,{"disambiguationData":[OD(0.0)],"derivedFrom":[makeQuery(id+"F5.opExtrude","SWEPT_FACE",FACE,{"disambiguationData":[OSD([sQuery(id+"F4.wireOp",EDGE,"E44")])]}),makeQuery(id+"F8.opExtrude","SWEPT_FACE",FACE,{"disambiguationData":[OSD([sQuery(id+"F7.wireOp",EDGE,"E81")])]})]});
            fillet(context, id + "F14", {"entities" : qUnion([Q0, Q1, Q2, Q3, Q4, Q5]), "radius" : 3 * mm, "tangentPropagation" : true, "allowEdgeOverflow" : false});
        }
        {
            var Q0;
            Q0=makeQuery(id+"F1.opExtrude","CAP_EDGE",EDGE,{"disambiguationData":[OSD([sQuery(id+"F0.wireOp",EDGE,"E1.bottom")])],"isStart":false});
            fillet(context, id + "F15", {"entities" : qUnion([Q0]), "radius" : 2 * mm, "tangentPropagation" : true, "allowEdgeOverflow" : false});
        }
        {
            var Q0;
            Q0 = qSketchRegion(id + "F0", true);
            var Q1;
            Q1=makeQuery(id+"F0.imprint","IMPRINT",FACE,{"disambiguationData":[TD([[makeQuery(id+"F0.imprint","IMPRINT",EDGE,{"derivedFrom":sQuery(id+"F0.wireOp",EDGE,"E12")}),-1.0]])]});
            var Q2;
            Q2=makeQuery(id+"F2.opExtrude","CAP_FACE",FACE,{"disambiguationData":[OSD([sQuery(id+"F0.wireOp",EDGE,"E12"),sQuery(id+"F0.wireOp",EDGE,"E13"),sQuery(id+"F0.wireOp",EDGE,"E14"),sQuery(id+"F0.wireOp",EDGE,"E15"),sQuery(id+"F0.wireOp",EDGE,"E17.filletArc"),sQuery(id+"F0.wireOp",EDGE,"E18.filletArc"),sQuery(id+"F0.wireOp",EDGE,"E19.filletArc"),sQuery(id+"F0.wireOp",EDGE,"E20.filletArc"),sQuery(id+"F0.wireOp",EDGE,"E25.0"),sQuery(id+"F0.wireOp",EDGE,"E25.1"),sQuery(id+"F0.wireOp",EDGE,"E25.2"),sQuery(id+"F0.wireOp",EDGE,"E25.3"),sQuery(id+"F0.wireOp",EDGE,"E25.4"),sQuery(id+"F0.wireOp",EDGE,"E25.5"),sQuery(id+"F0.wireOp",EDGE,"E25.6"),sQuery(id+"F0.wireOp",EDGE,"E25.7")])],"isStart":false});
            extrude(context, id + "F16", {"entities" : qUnion([Q0, Q1]), "endBound" : BoundingType.UP_TO_SURFACE, "depth" : 25 * mm, "endBoundEntityFace" : qUnion([Q2]), "offsetDistance" : 25 * mm});
        }
    });
